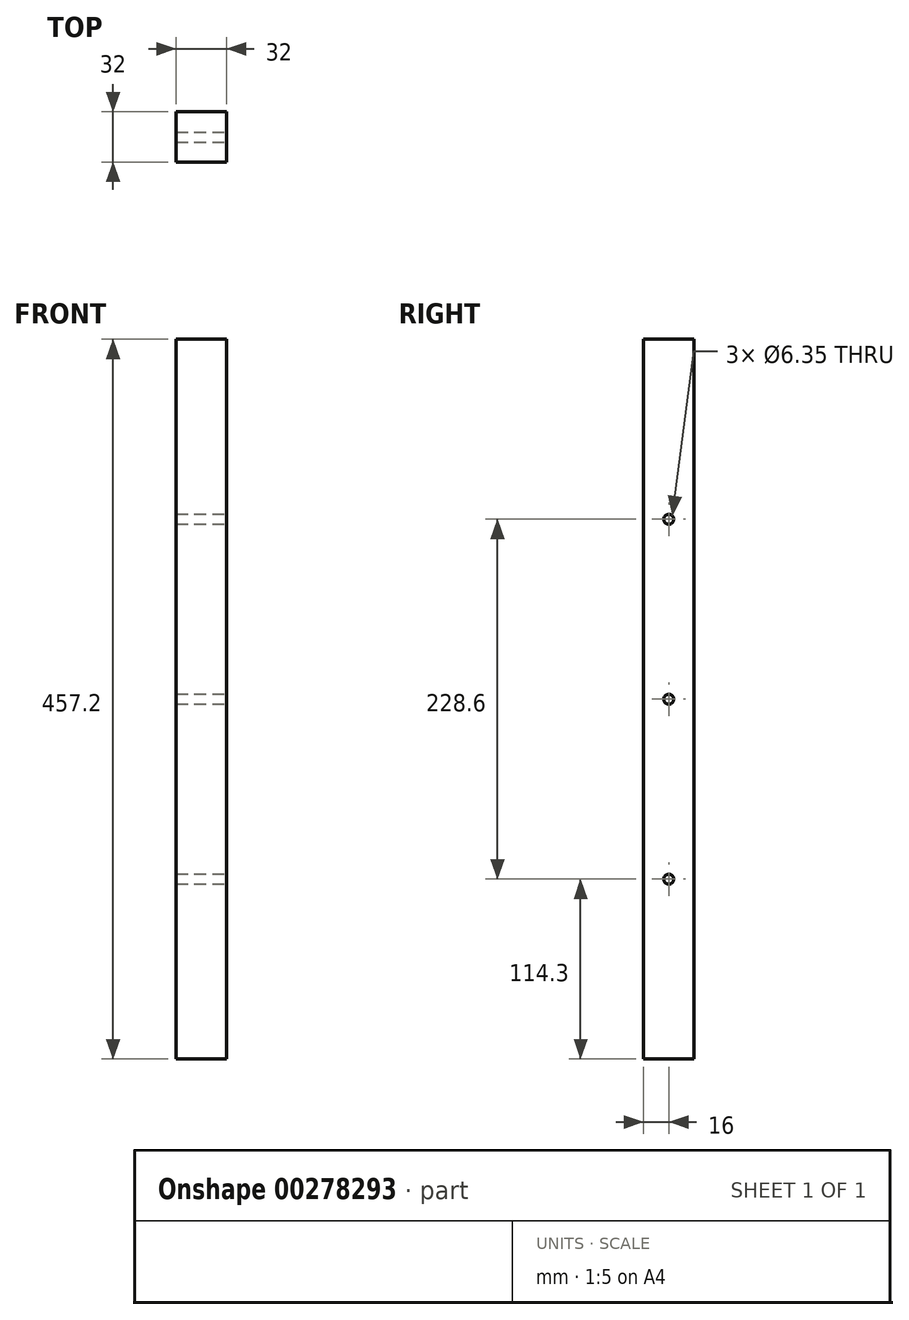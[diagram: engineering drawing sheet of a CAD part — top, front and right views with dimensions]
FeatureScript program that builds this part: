
annotation { "Feature Type Name" : "Feature", "Feature Type Description" : "" }
export const myFeature = defineFeature(function(context is Context, id is Id, definition is map)
    precondition{}
    {
        {
            var Q0;
            Q0=qCreatedBy(makeId("Top.planeOp"),FACE);
            var sketch = newSketch(context, id + "F0", { "sketchPlane" : qUnion([Q0])});
            skLineSegment(sketch, "E0.bottom", {"start": v(-16, -16) * mm, "end": v(16, -16) * mm});
            skLineSegment(sketch, "E0.top", {"start": v(-16, 16) * mm, "end": v(16, 16) * mm});
            skLineSegment(sketch, "E0.left", {"start": v(-16, -16) * mm, "end": v(-16, 16) * mm});
            skLineSegment(sketch, "E0.right", {"start": v(16, -16) * mm, "end": v(16, 16) * mm});
            skPoint(sketch, "E0.middle", {"position": v(0, 0) * mm});
            skSolve(sketch);
        }
        {
            var Q0;
            Q0 = qSketchRegion(id + "F0", true);
            extrude(context, id + "F1", {"entities" : qUnion([Q0]), "depth" : 457.2 * mm});
        }
        {
            var Q0;
            Q0=makeQuery(id+"F1.opExtrude","SWEPT_FACE",FACE,{"disambiguationData":[OSD([sQuery(id+"F0.wireOp",EDGE,"E0.right")])]});
            var sketch = newSketch(context, id + "F2", { "sketchPlane" : qUnion([Q0])});
            skLineSegment(sketch, "E1", {"start": v(0, 0) * mm, "end": v(0, 114.3) * mm});
            skPoint(sketch, "E1.endSnap0", {"position": v(0, 0) * mm});
            skLineSegment(sketch, "E2", {"start": v(0, 114.3) * mm, "end": v(0, 228.6) * mm});
            skCircle(sketch, "E3", {"center": v(0, 228.6) * mm, "radius": 3.18 * mm});
            skCircle(sketch, "E4", {"center": v(0, 114.3) * mm, "radius": 3.18 * mm});
            skLineSegment(sketch, "E5", {"start": v(0, 228.6) * mm, "end": v(0, 342.9) * mm});
            skCircle(sketch, "E6", {"center": v(0, 342.9) * mm, "radius": 3.18 * mm});
            skSolve(sketch);
        }
        {
            var Q0;
            Q0 = qSketchRegion(id + "F2", true);
            extrude(context, id + "F3", {"entities" : qUnion([Q0]), "operationType" : NewBodyOperationType.REMOVE, "endBound" : BoundingType.THROUGH_ALL, "oppositeDirection" : true, "depth" : 25 * mm});
        }
    });
